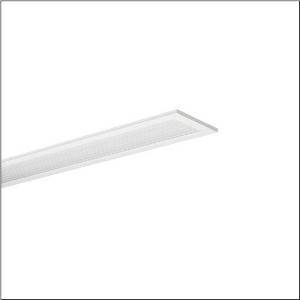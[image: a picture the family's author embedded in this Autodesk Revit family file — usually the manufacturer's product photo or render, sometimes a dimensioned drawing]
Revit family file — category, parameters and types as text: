
# Revit family: apollon_21_linear_51mq16wm2414
name_source: partatom
category: Lighting Fixtures
units: mm (PartAtom-declared; Revit-internal decimal feet)

## family parameters
Cut with Voids When Loaded = No
Host = Face
Light Source = No
Part Type = Normal
Room Calculation Point = No
Round Connector Dimension = Use Diameter
Shared = No

## types (1)
- --- (1 x LED, 4380 lm, 29.4 W, 4000K)
    Apparent Load = 29 VA
    CIE Flux Codes = 64 88 97 100 100
    Color Rendering = 80
    Color Temperature = 4000K
    Default Elevation = 1800 mm
    Description = Apollon 21 linear, office luminaire, primary optical cover: micro prismatic cover, of PMMA, CAT 2 (L<= 3000cd/m²), light emission: direct distribution, primary light characteristic: symmetric, installation type: lay-in mounting, LED, rated luminous flux: 3.520lm, luminous efficacy: 151lm/W, light colour: 840, colour temperature: 4000K, control gear: ON/OFF Multilumen, with terminal, 3-pole, mains connection: 220..240V, AC/DC, 0/50..60Hz, rated input power: 23.4W, housing, of aluminium, coated, traffic white (RAL 9016), length: 1.545mm, width: 179mm, height: 55mm, recess depth: 180mm, housing upper side, of sheet steel, galvanised, protection rating (complete): IP20, protection rating (lamp compartment, on room side): IP50, insulation class (complete): insulation class II (safety insulation), certification: CE, ENEC, impact resistance: IK03, permissible operating ambient temperature: -20..+45°C, permissible storage temperature: -40..+80°C, standard: EN 60598-2-22, packaging unit: 1 piece
    Height = 0 mm  [stored 0 ft]
    Lamp = 1 x LED
    Lamp Light Flux = 4380 lm
    Lamp Power = 29.4 W
    Lamp count = 1
    Length = 1545 mm
    Luminous efficacy = 149 lm/W
    Manufacturer = Siteco
    ModVariant = No
    Model = 51MQ16WM2414
    Mounting Place = Ceiling
    Mounting Type = Recessed
    Number of Poles = 1
    OnlyDefault = Yes
    Power Factor = 1
    Product Name = Apollon 21 linear
    Product group = office luminaire | ceiling recessed
    ProductGroupID = 401
    Protection Class = Protection class II
    Protection Degree = IP 20
    RLX_Detail_Level = 1
    RLX_Emergency_Light_Flux = 0 lm
    RLX_Emergency_Type = 0
    RLX_Emergency_Type_DB = No
    RlxData = <blob elided: 13917 chars, md5=35c803ce>
    Socket = socket
    Standby Power = 0 W
    System Light Flux = 4380 lm
    System Power = 29 W
    Type Comments = factory setting: luminous flux: 100 % | (ON | ON | ON) | 700 mA
    Type Image = l_1291018.jpg
    URL = http://relux.com
    VarID = @adj_064808
    Voltage = 0 V
    Weight = 0.00 kg
    Width = 179 mm

note: [stored X ft] marks values corroborated as IEEE doubles in the binary element streams (Revit-internal decimal feet)

## geometry (parser evidence)
native form markers: Sweep x9
no freeform markers — native parametric forms only
